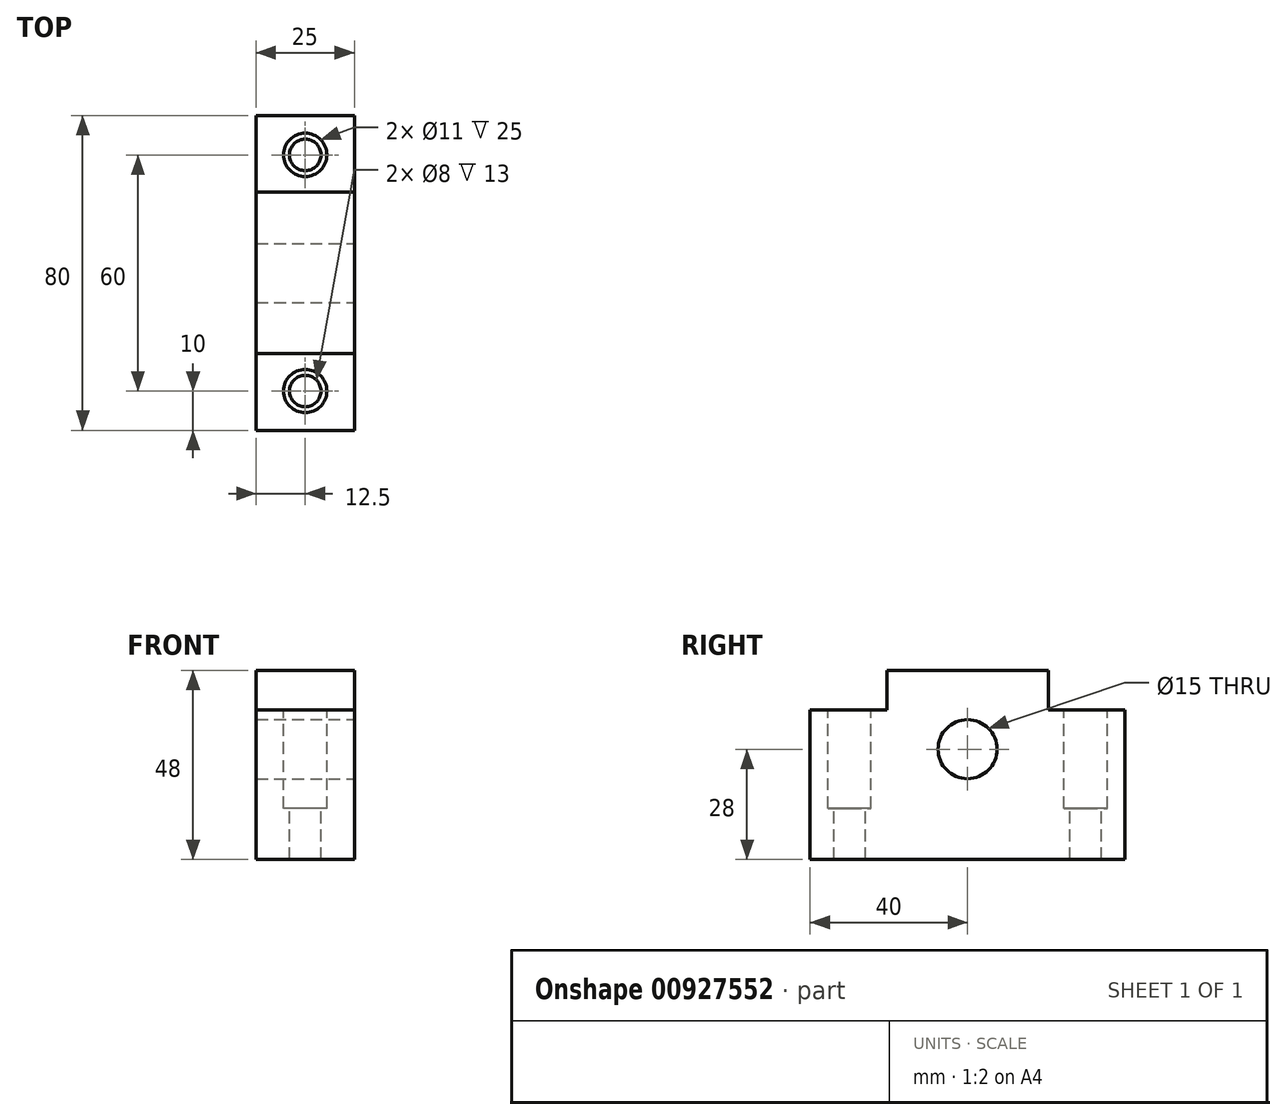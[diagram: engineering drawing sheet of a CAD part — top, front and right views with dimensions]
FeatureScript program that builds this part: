
annotation { "Feature Type Name" : "Feature", "Feature Type Description" : "" }
export const myFeature = defineFeature(function(context is Context, id is Id, definition is map)
    precondition{}
    {
        {
            var Q0;
            Q0=qCreatedBy(makeId("Right.planeOp"),FACE);
            var sketch = newSketch(context, id + "F0", { "sketchPlane" : qUnion([Q0])});
            skLineSegment(sketch, "E0.bottom", {"start": v(40, -24) * mm, "end": v(-40, -24) * mm});
            skLineSegment(sketch, "E0.top", {"start": v(40, 24) * mm, "end": v(-40, 24) * mm});
            skLineSegment(sketch, "E0.left", {"start": v(40, -24) * mm, "end": v(40, 24) * mm});
            skLineSegment(sketch, "E0.right", {"start": v(-40, -24) * mm, "end": v(-40, 24) * mm});
            skPoint(sketch, "E0.middle", {"position": v(0, 0) * mm});
            skSolve(sketch);
        }
        {
            var Q0;
            Q0 = qSketchRegion(id + "F0", true);
            extrude(context, id + "F1", {"entities" : qUnion([Q0]), "oppositeDirection" : true, "depth" : 25 * mm, "offsetDistance" : 25 * mm});
        }
        {
            var Q0;
            Q0=makeQuery(id+"F1.opExtrude","CAP_FACE",FACE,{"disambiguationData":[OSD([sQuery(id+"F0.wireOp",EDGE,"E0.bottom"),sQuery(id+"F0.wireOp",EDGE,"E0.top"),sQuery(id+"F0.wireOp",EDGE,"E0.left"),sQuery(id+"F0.wireOp",EDGE,"E0.right")])],"isStart":true});
            var sketch = newSketch(context, id + "F2", { "sketchPlane" : qUnion([Q0])});
            skLineSegment(sketch, "E1", {"start": v(20.5, 79.75) * mm, "end": v(20.5, 14) * mm});
            skLineSegment(sketch, "E2", {"start": v(20.5, 14) * mm, "end": v(111.61, 14) * mm});
            skLineSegment(sketch, "E3.MirrorCS", {"start": v(-20.5, 79.75) * mm, "end": v(-20.5, 14) * mm});
            skLineSegment(sketch, "E4.MirrorCS", {"start": v(-20.5, 14) * mm, "end": v(-111.61, 14) * mm});
            skSolve(sketch);
        }
        {
            var Q0;
            {var subQ0=sQuery(id+"F2.wireOp",EDGE,"E4.MirrorCS");var subQ1=sQuery(id+"F2.wireOp",EDGE,"E3.MirrorCS");var subQ2=makeQuery(id+"F2.imprint","INTERSECT",VERTEX,{"derivedFrom":[subQ1,subQ0]});Q0=makeQuery(id+"F2.imprint","IMPRINT",FACE,{"disambiguationData":[TD([[makeQuery(id+"F2.imprint","IMPRINT",EDGE,{"disambiguationData":[TD([[subQ2,1.0]])],"derivedFrom":subQ1}),-1.0]])]});}
            var Q1;
            {var subQ0=sQuery(id+"F2.wireOp",EDGE,"E2");var subQ1=sQuery(id+"F2.wireOp",EDGE,"E1");var subQ2=makeQuery(id+"F2.imprint","INTERSECT",VERTEX,{"derivedFrom":[subQ1,subQ0]});Q1=makeQuery(id+"F2.imprint","IMPRINT",FACE,{"disambiguationData":[TD([[makeQuery(id+"F2.imprint","IMPRINT",EDGE,{"disambiguationData":[TD([[subQ2,1.0]])],"derivedFrom":subQ1}),1.0]])]});}
            extrude(context, id + "F3", {"entities" : qUnion([Q0, Q1]), "operationType" : NewBodyOperationType.REMOVE, "endBound" : BoundingType.THROUGH_ALL, "oppositeDirection" : true, "depth" : 25 * mm, "offsetDistance" : 25 * mm});
        }
        {
            var Q0;
            Q0=makeQuery(id+"F1.opExtrude","CAP_FACE",FACE,{"disambiguationData":[OSD([sQuery(id+"F0.wireOp",EDGE,"E0.bottom"),sQuery(id+"F0.wireOp",EDGE,"E0.top"),sQuery(id+"F0.wireOp",EDGE,"E0.left"),sQuery(id+"F0.wireOp",EDGE,"E0.right")])],"isStart":true});
            var sketch = newSketch(context, id + "F4", { "sketchPlane" : qUnion([Q0])});
            skLineSegment(sketch, "E5", {"start": v(-73.6, 4) * mm, "end": v(86.61, 4) * mm, "construction": true});
            skCircle(sketch, "E6", {"center": v(0, 4) * mm, "radius": 7.5 * mm});
            skSolve(sketch);
        }
        {
            var Q0;
            Q0 = qSketchRegion(id + "F4", true);
            extrude(context, id + "F5", {"entities" : qUnion([Q0]), "operationType" : NewBodyOperationType.REMOVE, "endBound" : BoundingType.THROUGH_ALL, "oppositeDirection" : true, "depth" : 25 * mm, "offsetDistance" : 25 * mm});
        }
        {
            var Q0;
            Q0=makeQuery(id+"F3.boolean.opBoolean","COPY",FACE,{"derivedFrom":makeQuery(id+"F3.opExtrude","SWEPT_FACE",FACE,{"disambiguationData":[OSD([sQuery(id+"F2.wireOp",EDGE,"E2")])]})});
            var sketch = newSketch(context, id + "F6", { "sketchPlane" : qUnion([Q0])});
            skLineSegment(sketch, "E7", {"start": v(-12.5, 59.42) * mm, "end": v(-12.5, -64.84) * mm, "construction": true});
            skCircle(sketch, "E8", {"center": v(-12.5, 30) * mm, "radius": 5.5 * mm});
            skCircle(sketch, "E9.MirrorC", {"center": v(-12.5, -30) * mm, "radius": 5.5 * mm});
            skCircle(sketch, "E10", {"center": v(-12.5, 30) * mm, "radius": 4 * mm});
            skCircle(sketch, "E11.MirrorC", {"center": v(-12.5, -30) * mm, "radius": 4 * mm});
            skSolve(sketch);
        }
        {
            var Q0;
            Q0 = qSketchRegion(id + "F6", true);
            extrude(context, id + "F7", {"entities" : qUnion([Q0]), "operationType" : NewBodyOperationType.REMOVE, "oppositeDirection" : true, "depth" : 25 * mm, "offsetDistance" : 25 * mm});
        }
        {
            var Q0;
            Q0=makeQuery(id+"F7.boolean.opBoolean","SPLIT",FACE,{"disambiguationData":[TD([makeQuery(id+"F7.opExtrude","SWEPT_FACE",FACE,{"disambiguationData":[OSD([sQuery(id+"F6.wireOp",EDGE,"E10")])]})])],"derivedFrom":makeQuery(id+"F3.boolean.opBoolean","COPY",FACE,{"derivedFrom":makeQuery(id+"F3.opExtrude","SWEPT_FACE",FACE,{"disambiguationData":[OSD([sQuery(id+"F2.wireOp",EDGE,"E2")])]})})});
            var Q1;
            Q1=makeQuery(id+"F7.boolean.opBoolean","SPLIT",FACE,{"disambiguationData":[TD([makeQuery(id+"F7.opExtrude","SWEPT_FACE",FACE,{"disambiguationData":[OSD([sQuery(id+"F6.wireOp",EDGE,"E11.MirrorC")])]})])],"derivedFrom":makeQuery(id+"F3.boolean.opBoolean","COPY",FACE,{"derivedFrom":makeQuery(id+"F3.opExtrude","SWEPT_FACE",FACE,{"disambiguationData":[OSD([sQuery(id+"F2.wireOp",EDGE,"E4.MirrorCS")])]})})});
            extrude(context, id + "F8", {"entities" : qUnion([Q0, Q1]), "operationType" : NewBodyOperationType.REMOVE, "endBound" : BoundingType.THROUGH_ALL, "oppositeDirection" : true, "depth" : 25 * mm, "offsetDistance" : 25 * mm});
        }
    });
